# Revit family: KEUCO_14950019000
name_source: partatom
category: Sonderausstattung
revit_build: Autodesk Revit 2016 (Build: 20150220_1215(x64)
units: mm (PartAtom-declared; Revit-internal decimal feet)

## family parameters
Arbeitsebenenbasiert = Nein
Beim Laden mit Abzugskörper schneiden = Nein
Bemaßung runder Anschluss = Durchmesser verwenden
Gemeinsam genutzt = Nein
Immer vertikal = Ja
Raumberechnungspunkt = Nein
Teiletyp = Normal

## types (3) — shared parameters
Beschreibung = komplett mit Echtkristall-Glas
Gewicht = 382
Hersteller = KEUCO
Kategorie = ACC
Preisgruppe = 1
Serie = Plan
URL = https://www.keuco.com
Verwendung = WP

## per-type parameters (varying)
| type | Ausschreibungstext | Material Glas |
| 14950019000 | KEUCO PLAN Glashalter 14950019000
Hochglanzverchromter Glashalter 
in ästhetischem, funktionalem Design
komplett mit Echtkristall-Glas (Durchmesser 66 mm), 
leicht zu reinigen
Breite 66 mm, Höhe 116 mm, Ausladung 93 mm
Der Glashalter wird verdeckt angebracht
Lieferung inkl. korrosionsfreiem Befestigungsmaterial | Glas |
| 14950079000 | KEUCO PLAN Glashalter 14950079000
Glashalter aus hochwertigem Edelstahl 
in ästhetischem, funktionalem Design,
komplett mit Echtkristall-Glas (Durchmesser 66 mm), 
leicht zu reinigen
Breite 66 mm, Höhe 116 mm, Ausladung 93 mm
Der Glashalter wird verdeckt angebracht
Lieferung inkl. korrosionsfreiem Befestigungsmaterial | Glass |
| 14950179000 | KEUCO PLAN Glashalter 14950179000
Glashalter aus silber-eloxiertem Aluminium (E6 EV1)/verchromt 
in ästhetischem, funktionalem Design,
komplett mit Echtkristall-Glas (Durchmesser 66 mm), 
leicht zu reinigen
Die Wandhalterung ist als Design-Element hochglanzverchromt
Breite 66 mm, Höhe 116 mm, Ausladung 93 mm
Der Glashalter wird verdeckt angebracht
Lieferung inkl. korrosionsfreiem Befestigungsmaterial | Glass |

note: column(s) folded — value = type name in every type: Artikelnummer

## geometry (parser evidence)
native form markers: Blend x2, Sweep x3
no freeform markers — native parametric forms only
